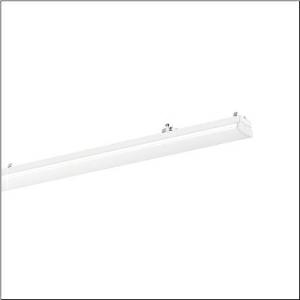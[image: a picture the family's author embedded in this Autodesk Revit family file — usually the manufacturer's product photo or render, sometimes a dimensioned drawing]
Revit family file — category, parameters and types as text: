
# Revit family: licross_11_recessed_opal_ho_51tl1ddv4m1m
name_source: partatom
category: Lighting Fixtures
units: mm (PartAtom-declared; Revit-internal decimal feet)

## family parameters
Cut with Voids When Loaded = No
Host = Face
Light Source = No
Part Type = Normal
Room Calculation Point = No
Round Connector Dimension = Use Diameter
Shared = No

## types (1)
- --- (1 x LED, 26350 lm, 150.5 W, 4000K)
    Apparent Load = 150 VA
    CIE Flux Codes = 44 73 91 87 100
    Color Rendering = 80
    Color Temperature = 4000K
    Default Elevation = 1800 mm
    Description = Licross 11 recessed opal HO, luminaire insert, of sheet steel, coil coated, white, length: 2.250mm, width: 76mm, height: 87mm, LED rated luminous flux: 26.350lm, light colour: 840, SDCM (Standard Deviation of Colour Matching)MacAdam ≤ 2 SDCM (initial), control gear: DALI 2, with plug, 5-pole, with phase selection, mains connection: 220..240V, AC, 50/60Hz, rated input power: 151W, internal wiring halogen-free, primary optical cover: cover, of PMMA, light emission: direct with ceiling illumination distribution, primary light characteristic: symmetric, protection rating (complete): IP40, insulation class (complete): insulation class I (protective earthing), certification: CE, ENEC, VDE, UKCA, protection symbol: D if used in an environment without relevant dust loads with corresponding accessories, impact resistance: IK06, permissible ambient temperature for indoor applications: -40..+35°C, corresponds to IFS (International Featured Standards) requirements for safety and quality in the food industry, reducing of maximum allowable ambient temperature of 5°C with ceiling mounting, LABS conformity tested according to VDMA 24364:2018-05, The light source and the operating device comply with the requirements of the Ecodesign Regulation (EU) 2019/2020 and are replaceable in accordance with this regulation, packaging unit: 1 piece
    Height = 83 mm
    Lamp = 1 x LED
    Lamp Light Flux = 26350 lm
    Lamp Power = 150.5 W
    Lamp count = 1
    Length = 2250 mm
    Luminous efficacy = 175 lm/W
    Manufacturer = Siteco
    ModVariant = No
    Model = 51TL1DDV4M1M
    Mounting Place = Ceiling
    Mounting Type = Pendant
    Number of Poles = 1
    OnlyDefault = Yes
    Power Factor = 1
    Product Name = Licross 11 recessed opal HO
    Product group = luminaire insert | ceiling pendant
    ProductGroupID = 901
    Protection Class = Protection class I
    Protection Degree = IP 40
    RLX_Detail_Level = 1
    RLX_Emergency_Light_Flux = 0 lm
    RLX_Emergency_Type = 0
    RLX_Emergency_Type_DB = No
    RlxData = <blob elided: 27245 chars, md5=1f67b7fb>
    Socket = socket
    Standby Power = 0 W
    System Light Flux = 26350 lm
    System Power = 150 W
    Type Comments = factory setting: luminous flux: 100 % | dim-lin: 254 | 690 mA
    Type Image = l_1313666.jpg
    URL = http://relux.com
    VarID = @adj_084169
    Voltage = 0 V
    Weight = 0.00 kg
    Width = 76 mm

## geometry (parser evidence)
native form markers: Blend x4, Sweep x11
no freeform markers — native parametric forms only
